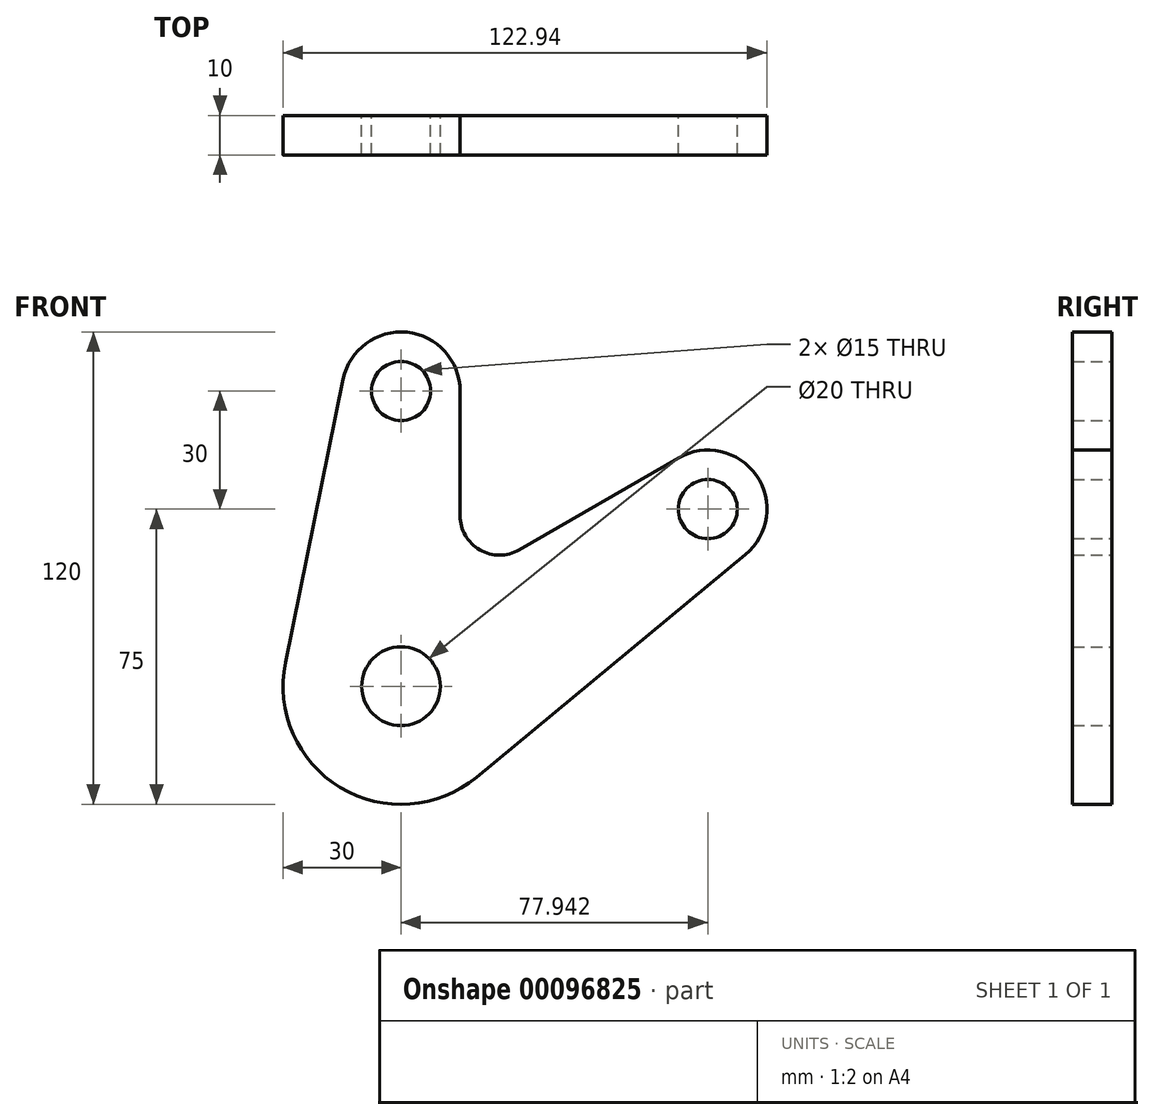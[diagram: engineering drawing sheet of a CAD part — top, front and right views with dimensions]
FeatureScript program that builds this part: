
annotation { "Feature Type Name" : "Feature", "Feature Type Description" : "" }
export const myFeature = defineFeature(function(context is Context, id is Id, definition is map)
    precondition{}
    {
        {
            var Q0;
            Q0=qCreatedBy(makeId("Front.planeOp"),FACE);
            var sketch = newSketch(context, id + "F0", { "sketchPlane" : qUnion([Q0])});
            skCircle(sketch, "E0", {"center": v(0, 0) * mm, "radius": 10 * mm});
            skCircle(sketch, "E1", {"center": v(0, 75) * mm, "radius": 7.5 * mm});
            skCircle(sketch, "E2", {"center": v(77.94, 45) * mm, "radius": 7.5 * mm});
            skLineSegment(sketch, "E3", {"start": v(15, 75) * mm, "end": v(15, 43.3) * mm});
            skArc(sketch, "E4", {"start": v(15, 43.3) * mm, "mid": v(20, 34.64) * mm, "end": v(30, 34.64) * mm});
            skLineSegment(sketch, "E5", {"start": v(30, 34.64) * mm, "end": v(70.44, 58) * mm});
            skArc(sketch, "E6", {"start": v(19.12, -23.12) * mm, "mid": v(-15.44, -25.72) * mm, "end": v(-29.4, 6) * mm});
            skLineSegment(sketch, "E7", {"start": v(-29.4, 6) * mm, "end": v(-14.7, 78) * mm});
            skArc(sketch, "E8", {"start": v(-14.7, 78) * mm, "mid": v(1.5, 89.92) * mm, "end": v(15, 75) * mm});
            skArc(sketch, "E9", {"start": v(70.44, 58) * mm, "mid": v(90.26, 53.56) * mm, "end": v(87.5, 33.44) * mm});
            skLineSegment(sketch, "E10", {"start": v(0, 0) * mm, "end": v(77.94, 45) * mm, "construction": true});
            skLineSegment(sketch, "E11", {"start": v(19.12, -23.12) * mm, "end": v(87.5, 33.44) * mm});
            skLineSegment(sketch, "E12", {"start": v(0, 0) * mm, "end": v(0, 75) * mm, "construction": true});
            skSolve(sketch);
        }
        {
            var Q0;
            Q0 = qSketchRegion(id + "F0", true);
            extrude(context, id + "F1", {"entities" : qUnion([Q0]), "depth" : 10 * mm});
        }
    });
